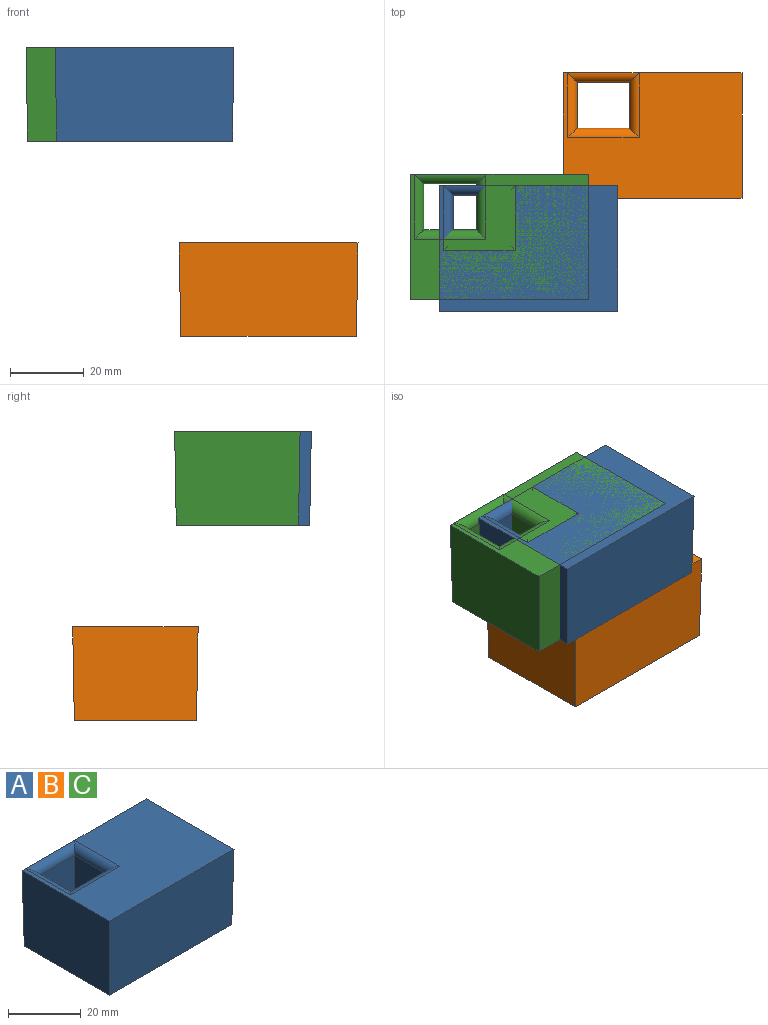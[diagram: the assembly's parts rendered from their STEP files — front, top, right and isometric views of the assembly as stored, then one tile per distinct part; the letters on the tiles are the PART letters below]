
ASSEMBLY  parts=3 mates=1
PART A: 14 faces, bbox 48.6x34.1x25.4 mm
  f0: plane 34.06x25.4mm, normal (-1,0,-0.02), area 854.1mm2, adj f1,f7,f8,f9
  f1: plane 48.57x25.4mm, normal (0,-1,-0.02), area 1222.7mm2, adj f0,f2,f8,f9
  f2: plane 34.06x25.4mm, normal (1,0,-0.02), area 854.1mm2, adj f1,f7,f8,f9
  f3: plane 22.86x14.3mm, normal (0,-1,0), area 326.9mm2, adj f4,f6,f9,f12
  f4: plane 22.86x12.51mm, normal (-1,0,0), area 286mm2, adj f3,f5,f9,f10
  f5: plane 22.86x14.3mm, normal (0,1,0), area 326.9mm2, adj f4,f6,f9,f11
  f6: plane 22.86x12.51mm, normal (1,0,0), area 286mm2, adj f3,f5,f9,f13
  f7: plane 48.57x25.4mm, normal (0,1,-0.02), area 1222.7mm2, adj f0,f2,f8,f9,f10,f12,f13
  f8: plane 48.57x34.06mm, normal (0,0,1), area 1314.1mm2, adj f0,f1,f2,f7,f10,f11,f13
  f9: plane 47.69x33.18mm, normal (0,0,-1), area 1403.3mm2, adj f0,f1,f2,f3,f4,f5,f6,f7
  f10: cylinder r=2.54mm len=17.57mm, axis (0,1,0), area 57.3mm2, adj f4,f7,f8,f11,f12
  f11: cylinder r=2.54mm len=19.38mm, axis (1,0,0), area 64.4mm2, adj f5,f8,f10,f13
  f12: cylinder r=2.54mm len=19.35mm, axis (-1,0,0), area 64.1mm2, adj f3,f7,f10,f13
  f13: cylinder r=2.54mm len=17.57mm, axis (0,-1,0), area 57.3mm2, adj f6,f7,f8,f11,f12
PART B: same geometry as A
PART C: same geometry as A
PLACE A t=(46.77,6.84,21.26)mm fixed
PLACE B t=(80.46,37.58,-31.81)mm
PLACE C t=(38.87,9.89,21.26)mm
MATE fastened A.f9 <-> C.f9  axis (0,0,-1) through (46.77,6.84,21.26)mm
